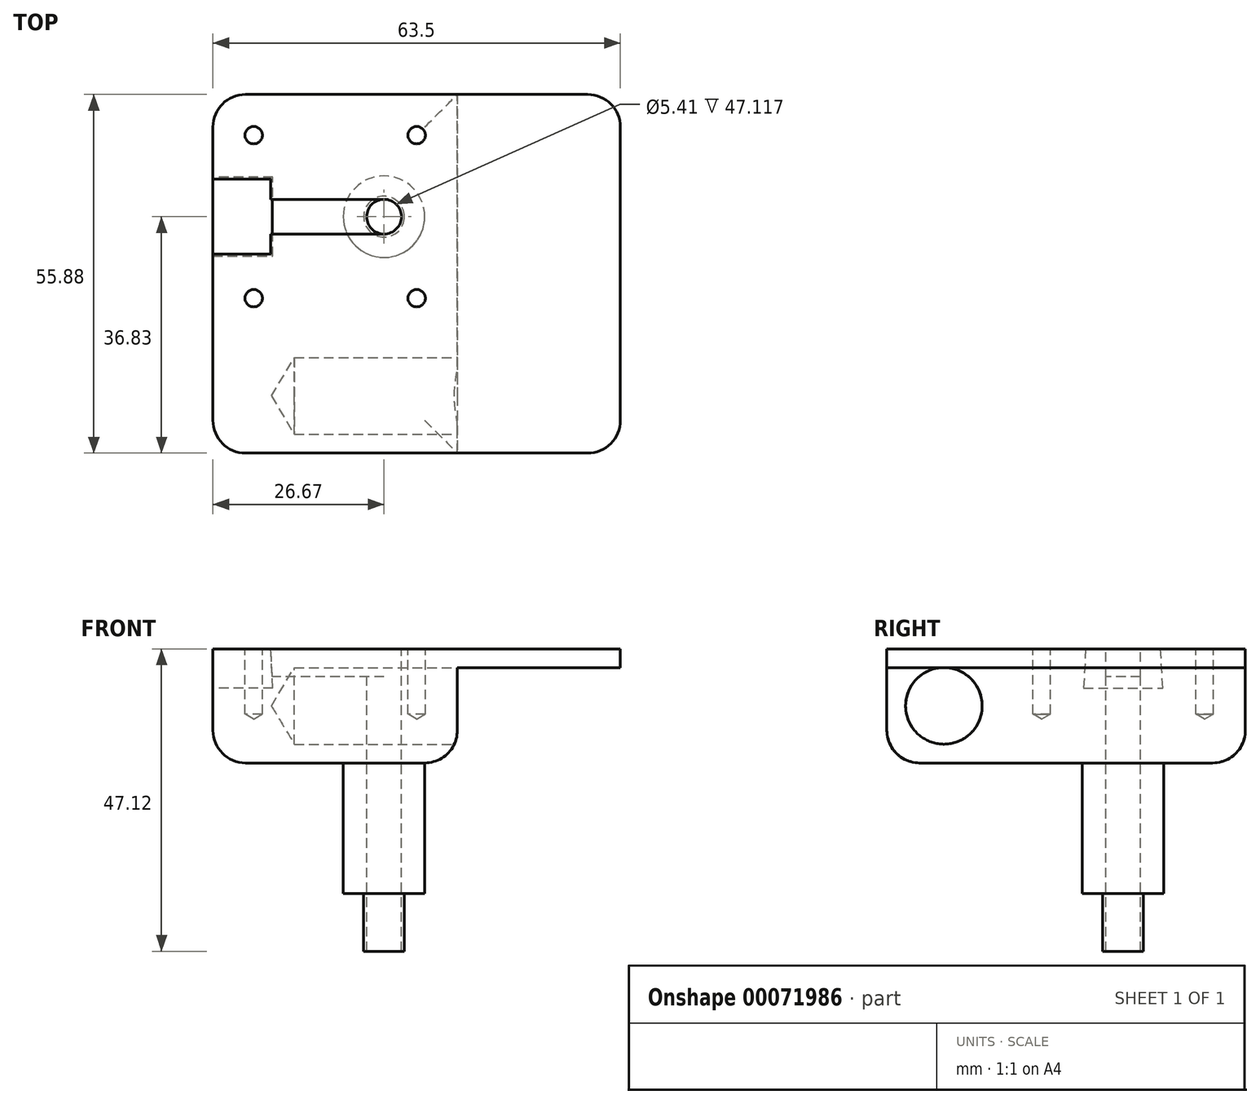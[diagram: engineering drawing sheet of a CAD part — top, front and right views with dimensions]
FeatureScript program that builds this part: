
annotation { "Feature Type Name" : "Feature", "Feature Type Description" : "" }
export const myFeature = defineFeature(function(context is Context, id is Id, definition is map)
    precondition{}
    {
        {
            var Q0;
            Q0=qCreatedBy(makeId("Front.planeOp"),FACE);
            var sketch = newSketch(context, id + "F0", { "sketchPlane" : qUnion([Q0])});
            skLineSegment(sketch, "E0.bottom", {"start": v(-19.05, 6.35) * mm, "end": v(19.05, 6.35) * mm});
            skLineSegment(sketch, "E0.top", {"start": v(-19.05, -6.35) * mm, "end": v(19.05, -6.35) * mm});
            skLineSegment(sketch, "E0.left", {"start": v(-19.05, 6.35) * mm, "end": v(-19.05, -6.35) * mm});
            skLineSegment(sketch, "E0.right", {"start": v(19.05, 6.35) * mm, "end": v(19.05, -6.35) * mm});
            skSolve(sketch);
        }
        {
            var Q0;
            Q0=makeQuery(id+"F0.imprint","IMPRINT",FACE,{"disambiguationData":[TD([[makeQuery(id+"F0.imprint","IMPRINT",EDGE,{"derivedFrom":sQuery(id+"F0.wireOp",EDGE,"E0.bottom")}),-1.0]])]});
            extrude(context, id + "F1", {"entities" : qUnion([Q0]), "endBound" : BoundingType.SYMMETRIC, "depth" : 38.1 * mm});
        }
        {
            var Q0;
            Q0=makeQuery(id+"F1.opExtrude","SWEPT_FACE",FACE,{"disambiguationData":[OSD([sQuery(id+"F0.wireOp",EDGE,"E0.bottom")])]});
            var sketch = newSketch(context, id + "F2", { "sketchPlane" : qUnion([Q0])});
            skCircle(sketch, "E1", {"center": v(7.62, 0) * mm, "radius": 6.35 * mm});
            skCircle(sketch, "E2", {"center": v(7.62, 0) * mm, "radius": 2.7 * mm});
            skLineSegment(sketch, "E3", {"start": v(7.62, 2.7) * mm, "end": v(-19.05, 2.7) * mm});
            skLineSegment(sketch, "E4", {"start": v(7.62, -2.7) * mm, "end": v(-19.05, -2.7) * mm});
            skLineSegment(sketch, "E5.bottom", {"start": v(-19.05, 5.84) * mm, "end": v(-10.03, 5.84) * mm});
            skLineSegment(sketch, "E5.top", {"start": v(-19.05, -5.84) * mm, "end": v(-10.03, -5.84) * mm});
            skLineSegment(sketch, "E5.left", {"start": v(-19.05, 5.84) * mm, "end": v(-19.05, -5.84) * mm});
            skLineSegment(sketch, "E5.right", {"start": v(-10.03, 5.84) * mm, "end": v(-10.03, -5.84) * mm});
            skSolve(sketch);
        }
        {
            var Q0;
            {var subQ5=sQuery(id+"F2.wireOp",EDGE,"E5.bottom");Q0=makeQuery(id+"F2.imprint","IMPRINT",FACE,{"disambiguationData":[TD([[makeQuery(id+"F2.imprint","IMPRINT",EDGE,{"derivedFrom":subQ5}),-1.0]])]});}
            var Q1;
            {var subQ0=sQuery(id+"F2.wireOp",EDGE,"E5.left");var subQ1=sQuery(id+"F2.wireOp",EDGE,"E3");var subQ2=makeQuery(id+"F2.imprint","INTERSECT",VERTEX,{"derivedFrom":[subQ1,subQ0]});Q1=makeQuery(id+"F2.imprint","IMPRINT",FACE,{"disambiguationData":[TD([[makeQuery(id+"F2.imprint","IMPRINT",EDGE,{"disambiguationData":[TD([[subQ2,1.0]])],"derivedFrom":subQ1}),1.0]])]});}
            var Q2;
            {var subQ5=sQuery(id+"F2.wireOp",EDGE,"E5.top");Q2=makeQuery(id+"F2.imprint","IMPRINT",FACE,{"disambiguationData":[TD([[makeQuery(id+"F2.imprint","IMPRINT",EDGE,{"derivedFrom":subQ5}),1.0]])]});}
            var Q3;
            Q3=sQuery(id+"F2.wireOp",EDGE,"E5.right");
            var Q4;
            Q4=sQuery(id+"F2.wireOp",EDGE,"E5.top");
            var Q5;
            Q5=sQuery(id+"F2.wireOp",EDGE,"E5.bottom");
            var Q6;
            Q6=sQuery(id+"F2.wireOp",EDGE,"E5.left");
            extrude(context, id + "F3", {"entities" : qUnion([Q0, Q1, Q2]), "operationType" : NewBodyOperationType.REMOVE, "surfaceEntities" : qUnion([Q3, Q4, Q5, Q6]), "oppositeDirection" : true, "depth" : 6.1 * mm, "hasDraft" : true, "draftAngle" : 3 * degree});
        }
        {
            var Q0;
            {var subQ5=sQuery(id+"F2.wireOp",EDGE,"E5.bottom");Q0=makeQuery(id+"F2.imprint","IMPRINT",FACE,{"disambiguationData":[TD([[makeQuery(id+"F2.imprint","IMPRINT",EDGE,{"derivedFrom":subQ5}),-1.0]])]});}
            var Q1;
            {var subQ5=sQuery(id+"F2.wireOp",EDGE,"E5.top");Q1=makeQuery(id+"F2.imprint","IMPRINT",FACE,{"disambiguationData":[TD([[makeQuery(id+"F2.imprint","IMPRINT",EDGE,{"derivedFrom":subQ5}),1.0]])]});}
            var Q2;
            {var subQ0=sQuery(id+"F2.wireOp",EDGE,"E3");var subQ1=sQuery(id+"F2.wireOp",EDGE,"E1");var subQ2=makeQuery(id+"F2.imprint","INTERSECT",VERTEX,{"derivedFrom":[subQ1,subQ0]});Q2=makeQuery(id+"F2.imprint","IMPRINT",FACE,{"disambiguationData":[TD([[makeQuery(id+"F2.imprint","IMPRINT",EDGE,{"disambiguationData":[TD([[subQ2,-1.0]])],"derivedFrom":subQ1}),1.0]])]});}
            var Q3;
            {var subQ0=sQuery(id+"F2.wireOp",EDGE,"E3");var subQ1=sQuery(id+"F2.wireOp",EDGE,"E1");var subQ2=makeQuery(id+"F2.imprint","INTERSECT",VERTEX,{"derivedFrom":[subQ1,subQ0]});Q3=makeQuery(id+"F2.imprint","IMPRINT",FACE,{"disambiguationData":[TD([[makeQuery(id+"F2.imprint","IMPRINT",EDGE,{"disambiguationData":[TD([[subQ2,-1.0]])],"derivedFrom":subQ1}),-1.0]])]});}
            var Q4;
            {var subQ0=sQuery(id+"F2.wireOp",EDGE,"E5.left");var subQ1=sQuery(id+"F2.wireOp",EDGE,"E3");var subQ2=makeQuery(id+"F2.imprint","INTERSECT",VERTEX,{"derivedFrom":[subQ1,subQ0]});Q4=makeQuery(id+"F2.imprint","IMPRINT",FACE,{"disambiguationData":[TD([[makeQuery(id+"F2.imprint","IMPRINT",EDGE,{"disambiguationData":[TD([[subQ2,1.0]])],"derivedFrom":subQ1}),1.0]])]});}
            extrude(context, id + "F4", {"entities" : qUnion([Q0, Q1, Q2, Q3, Q4]), "operationType" : NewBodyOperationType.REMOVE, "oppositeDirection" : true, "depth" : 4.32 * mm});
        }
        {
            var Q0;
            {var subQ0=sQuery(id+"F2.wireOp",EDGE,"E2");var subQ1=makeQuery(id+"F2.imprint","INTERSECT",VERTEX,{"derivedFrom":[subQ0,sQuery(id+"F2.wireOp",EDGE,"E3")]});Q0=makeQuery(id+"F2.imprint","IMPRINT",FACE,{"disambiguationData":[TD([[makeQuery(id+"F2.imprint","IMPRINT",EDGE,{"disambiguationData":[TD([[subQ1,-1.0]])],"derivedFrom":subQ0}),1.0]])]});}
            var Q1;
            Q1=sQuery(id+"F2.wireOp",EDGE,"E2");
            extrude(context, id + "F5", {"entities" : qUnion([Q0]), "operationType" : NewBodyOperationType.REMOVE, "surfaceEntities" : qUnion([Q1]), "endBound" : BoundingType.THROUGH_ALL, "oppositeDirection" : true, "depth" : 25.4 * mm});
        }
        {
            var Q0;
            {var subQ6=sQuery(id+"F2.wireOp",EDGE,"E5.bottom");Q0=makeQuery(id+"F2.imprint","IMPRINT",FACE,{"disambiguationData":[TD([[makeQuery(id+"F2.imprint","IMPRINT",EDGE,{"derivedFrom":subQ6}),1.0]])]});}
            var sketch = newSketch(context, id + "F6", { "sketchPlane" : qUnion([Q0])});
            skLineSegment(sketch, "E6", {"start": v(-12.7, 12.7) * mm, "end": v(12.7, 12.7) * mm});
            skLineSegment(sketch, "E7.MirrorCS", {"start": v(-12.7, -12.7) * mm, "end": v(12.7, -12.7) * mm});
            skSolve(sketch);
        }
        {
            var Q0;
            Q0=makeQuery(id+"F1.opExtrude","SWEPT_FACE",FACE,{"disambiguationData":[OSD([sQuery(id+"F0.wireOp",EDGE,"E0.top")])]});
            var sketch = newSketch(context, id + "F7", { "sketchPlane" : qUnion([Q0])});
            skCircle(sketch, "E8", {"center": v(7.62, 0) * mm, "radius": 6.35 * mm});
            skSolve(sketch);
        }
        {
            var Q0;
            Q0=makeQuery(id+"F7.imprint","IMPRINT",FACE,{"disambiguationData":[TD([[makeQuery(id+"F7.imprint","IMPRINT",EDGE,{"derivedFrom":sQuery(id+"F7.wireOp",EDGE,"E8")}),1.0]])]});
            var Q1;
            Q1=sQuery(id+"F7.wireOp",EDGE,"E8");
            extrude(context, id + "F8", {"entities" : qUnion([Q0]), "operationType" : NewBodyOperationType.ADD, "surfaceEntities" : qUnion([Q1]), "depth" : 25.4 * mm});
        }
        {
            var Q0;
            Q0=makeQuery(id+"F8.opExtrude","CAP_FACE",FACE,{"disambiguationData":[OSD([sQuery(id+"F0.wireOp",EDGE,"E0.top"),sQuery(id+"F2.wireOp",EDGE,"E2"),sQuery(id+"F7.wireOp",EDGE,"E8")])],"isStart":false});
            var sketch = newSketch(context, id + "F9", { "sketchPlane" : qUnion([Q0])});
            skCircle(sketch, "E9", {"center": v(7.62, 0) * mm, "radius": 3.18 * mm});
            skSolve(sketch);
        }
        {
            var Q0;
            Q0=makeQuery(id+"F9.imprint","IMPRINT",FACE,{"disambiguationData":[TD([[makeQuery(id+"F9.imprint","IMPRINT",EDGE,{"derivedFrom":sQuery(id+"F9.wireOp",EDGE,"E9")}),1.0]])]});
            extrude(context, id + "F10", {"entities" : qUnion([Q0]), "operationType" : NewBodyOperationType.ADD, "depth" : 9.02 * mm});
        }
        {
            var Q0;
            Q0=makeQuery(id+"F1.opExtrude","CAP_FACE",FACE,{"disambiguationData":[OSD([sQuery(id+"F0.wireOp",EDGE,"E0.bottom"),sQuery(id+"F0.wireOp",EDGE,"E0.top"),sQuery(id+"F0.wireOp",EDGE,"E0.left"),sQuery(id+"F0.wireOp",EDGE,"E0.right")])],"isStart":false});
            extrude(context, id + "F11", {"entities" : qUnion([Q0]), "operationType" : NewBodyOperationType.ADD, "depth" : 17.78 * mm});
        }
        {
            var Q0;
            {var subQ0=sQuery(id+"F0.wireOp",EDGE,"E0.top");Q0=makeQuery(id+"F11.boolean.opBoolean","MERGE",FACE,{"derivedFrom":[makeQuery(id+"F1.opExtrude","SWEPT_FACE",FACE,{"disambiguationData":[OSD([subQ0])]}),makeQuery(id+"F11.opExtrude","SWEPT_FACE",FACE,{"disambiguationData":[OSD([subQ0])]})]});}
            extrude(context, id + "F12", {"entities" : qUnion([Q0]), "operationType" : NewBodyOperationType.ADD, "depth" : 5.08 * mm});
        }
        {
            var Q0;
            {var subQ0=sQuery(id+"F0.wireOp",EDGE,"E0.right");Q0=makeQuery(id+"F12.boolean.opBoolean","MERGE",FACE,{"derivedFrom":[makeQuery(id+"F11.boolean.opBoolean","MERGE",FACE,{"derivedFrom":[makeQuery(id+"F1.opExtrude","SWEPT_FACE",FACE,{"disambiguationData":[OSD([subQ0])]}),makeQuery(id+"F11.opExtrude","SWEPT_FACE",FACE,{"disambiguationData":[OSD([subQ0])]})]}),makeQuery(id+"F12.opExtrude","SWEPT_FACE",FACE,{"disambiguationData":[OSD([sQuery(id+"F0.wireOp",EDGE,"E0.top"),subQ0])]})]});}
            var sketch = newSketch(context, id + "F13", { "sketchPlane" : qUnion([Q0])});
            skLineSegment(sketch, "E10", {"start": v(0, 0) * mm, "end": v(-15.24, 0) * mm});
            skLineSegment(sketch, "E11", {"start": v(-15.24, 0) * mm, "end": v(-15.24, -2.54) * mm});
            skLineSegment(sketch, "E12", {"start": v(-36.83, -2.54) * mm, "end": v(-27.94, -2.54) * mm});
            skSolve(sketch);
        }
        {
            var Q0;
            Q0=sQuery(id+"F13.wireOp",VERTEX,"E12.end");
            var Q1;
            Q1=makeQuery(id+"F1.opExtrude","SWEPT_BODY",BODY,{"disambiguationData":[OSD([sQuery(id+"F0.wireOp",EDGE,"E0.bottom"),sQuery(id+"F0.wireOp",EDGE,"E0.top"),sQuery(id+"F0.wireOp",EDGE,"E0.left"),sQuery(id+"F0.wireOp",EDGE,"E0.right")])]});
            hole(context, id + "F14", {"style" : HoleStyle.SIMPLE, "holeDiameter" : 11.94 * mm, "endStyle" : HoleEndStyle.BLIND, "holeDepth" : 25.4 * mm, "locations" : qUnion([Q0]), "scope" : qUnion([Q1])});
        }
        {
            var Q0;
            {var subQ0=sQuery(id+"F0.wireOp",EDGE,"E0.right");var subQ1=sQuery(id+"F0.wireOp",EDGE,"E0.top");var subQ6=makeQuery(id+"F12.opExtrude","CAP_EDGE",EDGE,{"disambiguationData":[OSD([subQ1,subQ0])],"isStart":false});Q0=makeQuery(id+"F13.imprint","IMPRINT",FACE,{"disambiguationData":[TD([[makeQuery(id+"F13.imprint","IMPRINT",EDGE,{"derivedFrom":subQ6}),1.0]])]});}
            var sketch = newSketch(context, id + "F15", { "sketchPlane" : qUnion([Q0])});
            skLineSegment(sketch, "E13.bottom", {"start": v(19.05, 6.35) * mm, "end": v(-36.83, 6.35) * mm});
            skLineSegment(sketch, "E13.top", {"start": v(19.05, 3.43) * mm, "end": v(-36.83, 3.43) * mm});
            skLineSegment(sketch, "E13.left", {"start": v(19.05, 6.35) * mm, "end": v(19.05, 3.43) * mm});
            skLineSegment(sketch, "E13.right", {"start": v(-36.83, 6.35) * mm, "end": v(-36.83, 3.43) * mm});
            skSolve(sketch);
        }
        {
            var Q0;
            Q0=makeQuery(id+"F15.imprint","IMPRINT",FACE,{"disambiguationData":[TD([[makeQuery(id+"F15.imprint","IMPRINT",EDGE,{"derivedFrom":sQuery(id+"F15.wireOp",EDGE,"E13.bottom")}),-1.0]])]});
            extrude(context, id + "F16", {"entities" : qUnion([Q0]), "operationType" : NewBodyOperationType.ADD, "depth" : 25.4 * mm});
        }
        {
            var Q0;
            {var subQ0=sQuery(id+"F0.wireOp",EDGE,"E0.left");var subQ1=sQuery(id+"F0.wireOp",EDGE,"E0.top");Q0=makeQuery(id+"F12.boolean.opBoolean","MERGE",EDGE,{"derivedFrom":[makeQuery(id+"F11.opExtrude","CAP_EDGE",EDGE,{"disambiguationData":[OSD([subQ0])],"isStart":false}),makeQuery(id+"F12.opExtrude","SWEPT_EDGE",EDGE,{"disambiguationData":[OSD([subQ1,subQ0]),TDD([makeQuery(id+"F11.opExtrude","CAP_VERTEX",VERTEX,{"disambiguationData":[OSD([subQ1,subQ0])],"isStart":false})])]})]});}
            var Q1;
            Q1=makeQuery(id+"F16.opExtrude","CAP_EDGE",EDGE,{"disambiguationData":[OSD([sQuery(id+"F15.wireOp",EDGE,"E13.left")])],"isStart":false});
            var Q2;
            {var subQ0=sQuery(id+"F0.wireOp",EDGE,"E0.left");var subQ1=sQuery(id+"F0.wireOp",EDGE,"E0.top");Q2=makeQuery(id+"F12.boolean.opBoolean","MERGE",EDGE,{"derivedFrom":[makeQuery(id+"F1.opExtrude","CAP_EDGE",EDGE,{"disambiguationData":[OSD([subQ0])],"isStart":true}),makeQuery(id+"F12.opExtrude","SWEPT_EDGE",EDGE,{"disambiguationData":[OSD([subQ1,subQ0]),TDD([makeQuery(id+"F1.opExtrude","CAP_VERTEX",VERTEX,{"disambiguationData":[OSD([subQ1,subQ0])],"isStart":true})])]})]});}
            var Q3;
            Q3=makeQuery(id+"F12.opExtrude","CAP_EDGE",EDGE,{"disambiguationData":[OSD([sQuery(id+"F0.wireOp",EDGE,"E0.top"),sQuery(id+"F0.wireOp",EDGE,"E0.left")])],"isStart":false});
            var Q4;
            {var subQ0=sQuery(id+"F0.wireOp",EDGE,"E0.top");Q4=makeQuery(id+"F12.opExtrude","CAP_EDGE",EDGE,{"disambiguationData":[OSD([subQ0]),TDD([makeQuery(id+"F11.opExtrude","CAP_EDGE",EDGE,{"disambiguationData":[OSD([subQ0])],"isStart":false})])],"isStart":false});}
            var Q5;
            Q5=makeQuery(id+"F12.opExtrude","CAP_EDGE",EDGE,{"disambiguationData":[OSD([sQuery(id+"F0.wireOp",EDGE,"E0.top"),sQuery(id+"F0.wireOp",EDGE,"E0.right")])],"isStart":false});
            var Q6;
            {var subQ0=sQuery(id+"F0.wireOp",EDGE,"E0.top");Q6=makeQuery(id+"F12.opExtrude","CAP_EDGE",EDGE,{"disambiguationData":[OSD([subQ0]),TDD([makeQuery(id+"F1.opExtrude","CAP_EDGE",EDGE,{"disambiguationData":[OSD([subQ0])],"isStart":true})])],"isStart":false});}
            var Q7;
            Q7=makeQuery(id+"F16.opExtrude","CAP_EDGE",EDGE,{"disambiguationData":[OSD([sQuery(id+"F15.wireOp",EDGE,"E13.right")])],"isStart":false});
            fillet(context, id + "F17", {"entities" : qUnion([Q0, Q1, Q2, Q3, Q4, Q5, Q6, Q7]), "radius" : 5.08 * mm, "tangentPropagation" : true, "allowEdgeOverflow" : false});
        }
        {
            var Q0;
            Q0=sQuery(id+"F6.wireOp",VERTEX,"E6.start");
            var Q1;
            Q1=sQuery(id+"F6.wireOp",VERTEX,"E7.MirrorCS.start");
            var Q2;
            Q2=sQuery(id+"F6.wireOp",VERTEX,"E7.MirrorCS.end");
            var Q3;
            Q3=sQuery(id+"F6.wireOp",VERTEX,"E6.end");
            var Q4;
            Q4=makeQuery(id+"F1.opExtrude","SWEPT_BODY",BODY,{"disambiguationData":[OSD([sQuery(id+"F0.wireOp",EDGE,"E0.bottom"),sQuery(id+"F0.wireOp",EDGE,"E0.top"),sQuery(id+"F0.wireOp",EDGE,"E0.left"),sQuery(id+"F0.wireOp",EDGE,"E0.right")])]});
            hole(context, id + "F18", {"style" : HoleStyle.SIMPLE, "holeDiameter" : 2.7 * mm, "endStyle" : HoleEndStyle.BLIND, "holeDepth" : 10.16 * mm, "locations" : qUnion([Q0, Q1, Q2, Q3]), "scope" : qUnion([Q4])});
        }
    });
